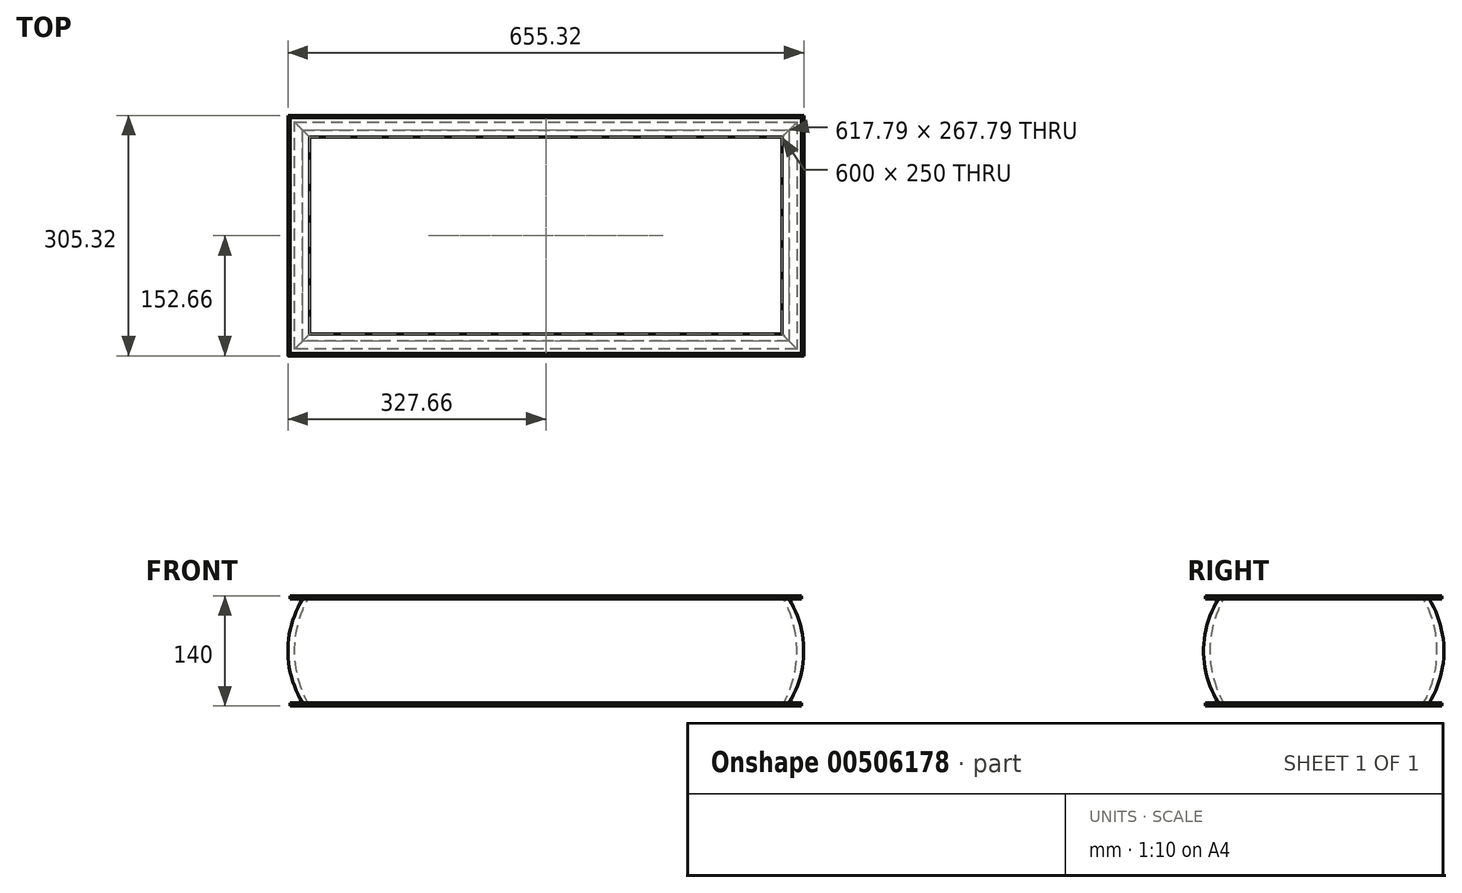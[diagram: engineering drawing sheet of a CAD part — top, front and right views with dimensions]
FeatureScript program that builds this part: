
annotation { "Feature Type Name" : "Feature", "Feature Type Description" : "" }
export const myFeature = defineFeature(function(context is Context, id is Id, definition is map)
    precondition{}
    {
        {
            var Q0;
            Q0=qCreatedBy(makeId("Top.planeOp"),FACE);
            var sketch = newSketch(context, id + "F0", { "sketchPlane" : qUnion([Q0])});
            skLineSegment(sketch, "E0.bottom", {"start": v(325, 150) * mm, "end": v(-325, 150) * mm});
            skLineSegment(sketch, "E0.top", {"start": v(325, -150) * mm, "end": v(-325, -150) * mm});
            skLineSegment(sketch, "E0.left", {"start": v(325, 150) * mm, "end": v(325, -150) * mm});
            skLineSegment(sketch, "E0.right", {"start": v(-325, 150) * mm, "end": v(-325, -150) * mm});
            skPoint(sketch, "E0.middle", {"position": v(0, 0) * mm});
            skSolve(sketch);
        }
        {
            var Q0;
            Q0=qCreatedBy(makeId("Right.planeOp"),FACE);
            var sketch = newSketch(context, id + "F1", { "sketchPlane" : qUnion([Q0])});
            skLineSegment(sketch, "E1.top", {"start": v(131.31, -70) * mm, "end": v(125, -70) * mm});
            skArc(sketch, "E2", {"start": v(133.9, -66) * mm, "mid": v(152.66, 0) * mm, "end": v(133.9, 66) * mm});
            skLineSegment(sketch, "E3.bottom", {"start": v(125, -70) * mm, "end": v(150, -70) * mm});
            skLineSegment(sketch, "E3.top", {"start": v(133.9, -66) * mm, "end": v(150, -66) * mm});
            skLineSegment(sketch, "E3.right", {"start": v(150, -70) * mm, "end": v(150, -66) * mm});
            skLineSegment(sketch, "E4.MirrorCS", {"start": v(131.31, 70) * mm, "end": v(125, 70) * mm});
            skLineSegment(sketch, "E5.MirrorCS", {"start": v(150, 70) * mm, "end": v(150, 66) * mm});
            skLineSegment(sketch, "E6.MirrorCS", {"start": v(125, 70) * mm, "end": v(150, 70) * mm});
            skLineSegment(sketch, "E7.MirrorCS", {"start": v(133.9, 66) * mm, "end": v(150, 66) * mm});
            skArc(sketch, "E8", {"start": v(125, -70) * mm, "mid": v(144.04, 0) * mm, "end": v(125, 70) * mm});
            skSolve(sketch);
        }
        {
            var Q0;
            Q0=makeQuery(id+"F1.imprint","IMPRINT",FACE,{"disambiguationData":[TD([[makeQuery(id+"F1.imprint","IMPRINT",EDGE,{"derivedFrom":sQuery(id+"F1.wireOp",EDGE,"E2")}),1.0]])]});
            var Q1;
            Q1=sQuery(id+"F1.wireOp",EDGE,"E2");
            var Q2;
            Q2=sQuery(id+"F1.wireOp",EDGE,"E6.MirrorCS");
            var Q3;
            Q3=sQuery(id+"F1.wireOp",EDGE,"E7.MirrorCS");
            var Q4;
            Q4=sQuery(id+"F1.wireOp",EDGE,"E5.MirrorCS");
            var Q5;
            Q5=sQuery(id+"F1.wireOp",EDGE,"E8");
            var Q6;
            Q6=sQuery(id+"F1.wireOp",EDGE,"E3.bottom");
            var Q7;
            Q7=sQuery(id+"F1.wireOp",EDGE,"E3.top");
            var Q8;
            Q8=sQuery(id+"F1.wireOp",EDGE,"E3.right");
            var Q9;
            Q9=sQuery(id+"F0.wireOp",EDGE,"E0.right");
            var Q10;
            Q10=sQuery(id+"F0.wireOp",EDGE,"E0.top");
            var Q11;
            Q11=sQuery(id+"F0.wireOp",EDGE,"E0.left");
            var Q12;
            Q12=sQuery(id+"F0.wireOp",EDGE,"E0.bottom");
            sweep(context, id + "F2", {"profiles" : qUnion([Q0]), "surfaceProfiles" : qUnion([Q1, Q2, Q3, Q4, Q5, Q6, Q7, Q8]), "path" : qUnion([Q9, Q10, Q11, Q12])});
        }
    });
